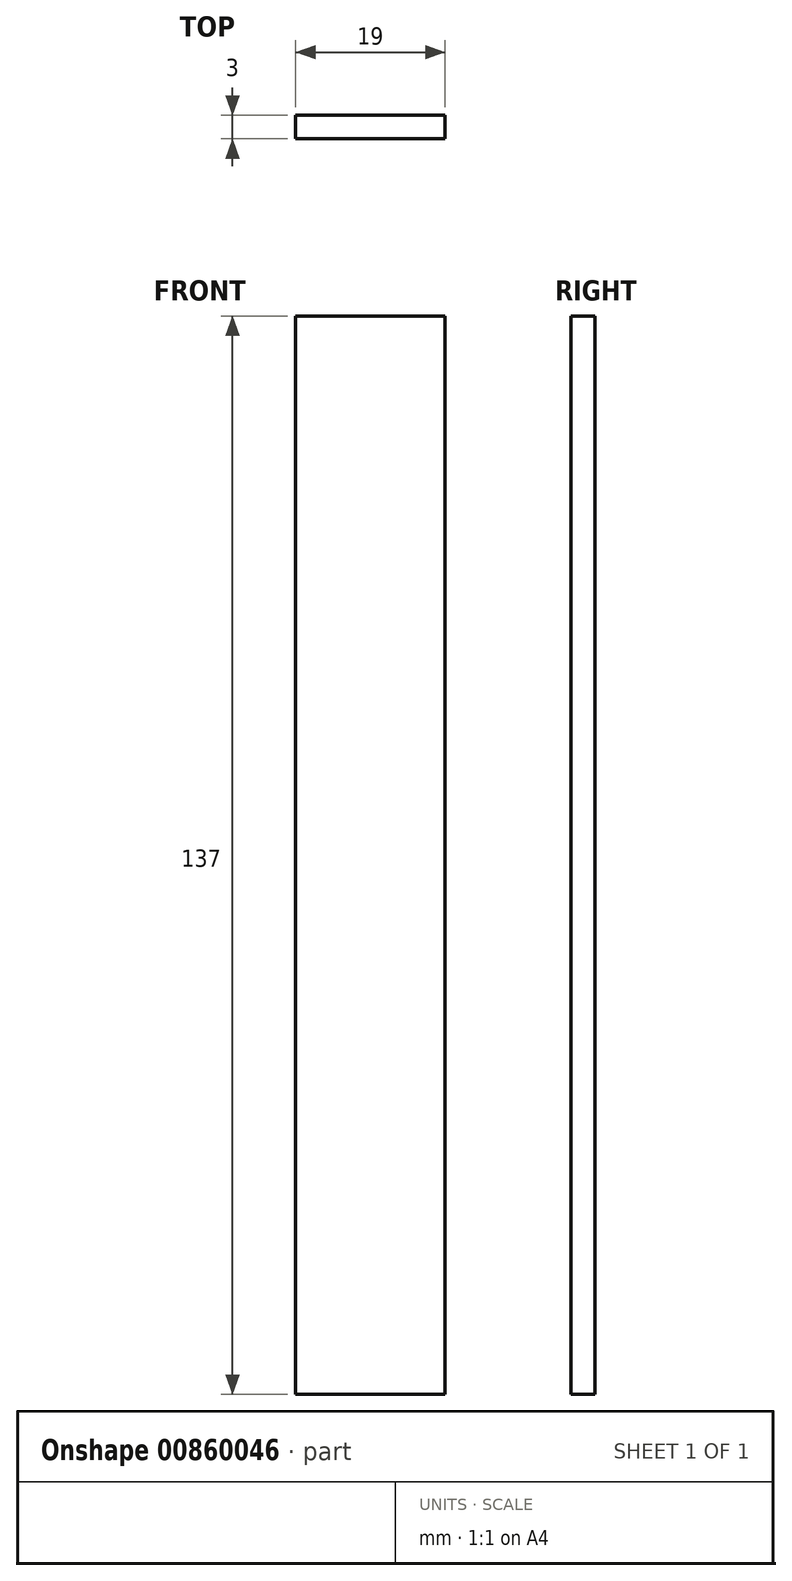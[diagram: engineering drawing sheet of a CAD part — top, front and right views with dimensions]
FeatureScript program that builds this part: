
annotation { "Feature Type Name" : "Feature", "Feature Type Description" : "" }
export const myFeature = defineFeature(function(context is Context, id is Id, definition is map)
    precondition{}
    {
        {
            var Q0;
            Q0=qCreatedBy(makeId("Top.planeOp"),FACE);
            var sketch = newSketch(context, id + "F0", { "sketchPlane" : qUnion([Q0])});
            skLineSegment(sketch, "E0.bottom", {"start": v(-9.47, 3) * mm, "end": v(9.53, 3) * mm});
            skLineSegment(sketch, "E0.top", {"start": v(-9.47, 0) * mm, "end": v(9.53, 0) * mm});
            skLineSegment(sketch, "E0.left", {"start": v(-9.47, 3) * mm, "end": v(-9.47, 0) * mm});
            skLineSegment(sketch, "E0.right", {"start": v(9.53, 3) * mm, "end": v(9.53, 0) * mm});
            skSolve(sketch);
        }
        {
            var Q0;
            Q0 = qSketchRegion(id + "F0", true);
            extrude(context, id + "F1", {"entities" : qUnion([Q0]), "depth" : 137 * mm, "offsetDistance" : 25 * mm});
        }
    });
